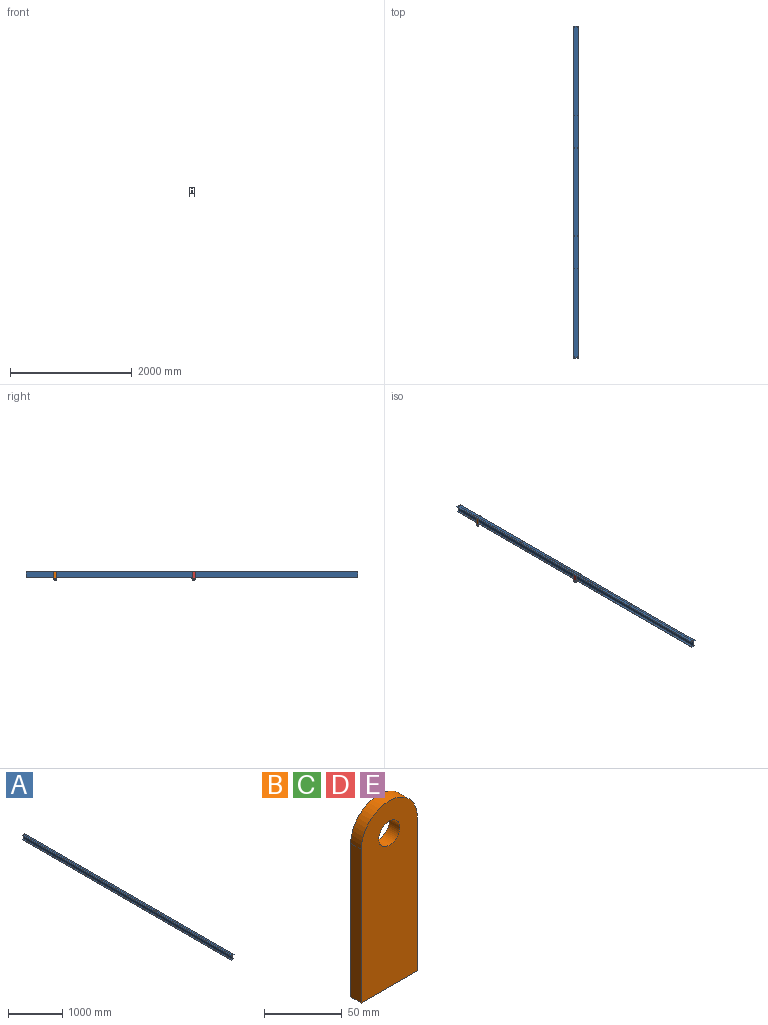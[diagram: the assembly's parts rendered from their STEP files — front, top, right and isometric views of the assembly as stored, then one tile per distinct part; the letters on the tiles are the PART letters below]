
ASSEMBLY  parts=5 mates=4
PART A: 26 faces, bbox 76.2x5448.3x101.6 mm
  f0: plane 5448.3x76.2mm, normal (0,0,1), area 414566.7mm2, adj f1,f11,f12,f13,f14,f15,f16,f17
  f1: plane 5448.3x4.32mm, normal (-1,0,0), area 23525.8mm2, adj f0,f2,f12,f13
  f2: plane 5448.3x35.94mm, normal (0,0,-1), area 195520.5mm2, adj f1,f3,f12,f13,f20,f21,f22,f23
  f3: plane 5448.3x92.96mm, normal (-1,0,0), area 506495.8mm2, adj f2,f4,f12,f13
  f4: plane 5448.3x32.23mm, normal (0,0,1), area 175618.2mm2, adj f3,f5,f12,f13
  f5: plane 5448.3x4.32mm, normal (-1,0,0), area 23525.8mm2, adj f4,f6,f12,f13
  f6: plane 5448.3x68.79mm, normal (0,0,-1), area 374762.1mm2, adj f5,f7,f12,f13
  f7: plane 5448.3x4.32mm, normal (1,0,0), area 23525.8mm2, adj f6,f8,f12,f13
  f8: plane 5448.3x32.23mm, normal (0,0,1), area 175618.2mm2, adj f7,f9,f12,f13
  f9: plane 5448.3x92.96mm, normal (1,0,0), area 506495.8mm2, adj f8,f10,f12,f13
  f10: plane 5448.3x35.94mm, normal (0,0,-1), area 195520.5mm2, adj f9,f11,f12,f13,f14,f15,f16,f17
  f11: plane 5448.3x4.32mm, normal (1,0,0), area 23525.8mm2, adj f0,f10,f12,f13
  f12: plane 101.6x76.2mm, normal (0,-1,0), area 1027.5mm2, adj f0,f1,f2,f3,f4,f5,f6,f7
  f13: plane 101.6x76.2mm, normal (0,1,0), area 1027.5mm2, adj f0,f1,f2,f3,f4,f5,f6,f7
  f14: cylinder r=3.97mm len=7.94mm, axis (0,0,1), area 107.7mm2, adj f0,f10
  f15: cylinder r=3.97mm len=7.94mm, axis (0,0,1), area 107.7mm2, adj f0,f10
  f16: cylinder r=3.97mm len=7.94mm, axis (0,0,1), area 107.7mm2, adj f0,f10
  f17: cylinder r=3.97mm len=7.94mm, axis (0,0,1), area 107.7mm2, adj f0,f10
  f18: cylinder r=3.97mm len=7.94mm, axis (0,0,1), area 107.7mm2, adj f0,f10
  f19: cylinder r=3.97mm len=7.94mm, axis (0,0,1), area 107.7mm2, adj f0,f10
  f20: cylinder r=3.97mm len=7.94mm, axis (0,0,1), area 107.7mm2, adj f0,f2
  f21: cylinder r=3.97mm len=7.94mm, axis (0,0,1), area 107.7mm2, adj f0,f2
  f22: cylinder r=3.97mm len=7.94mm, axis (0,0,1), area 107.7mm2, adj f0,f2
  f23: cylinder r=3.97mm len=7.94mm, axis (0,0,1), area 107.7mm2, adj f0,f2
  f24: cylinder r=3.97mm len=7.94mm, axis (0,0,1), area 107.7mm2, adj f0,f2
  f25: cylinder r=3.97mm len=7.94mm, axis (0,0,1), area 107.7mm2, adj f0,f2
PART B: 7 faces, bbox 50.8x9.5x146.1 mm
  f0: plane 120.65x9.53mm, normal (-1,0,0), area 1149.2mm2, adj f1,f4,f5,f6
  f1: plane 50.8x9.53mm, normal (0,0,-1), area 483.9mm2, adj f0,f2,f5,f6
  f2: plane 120.65x9.53mm, normal (1,0,0), area 1149.2mm2, adj f1,f4,f5,f6
  f3: cylinder r=9.53mm len=19.05mm, axis (0,1,0), area 570mm2, adj f5,f6
  f4: cylinder r=25.4mm len=50.8mm, axis (0,1,0), area 760.1mm2, adj f0,f2,f5,f6
  f5: plane 146.05x50.8mm, normal (0,-1,0), area 6857.4mm2, adj f0,f1,f2,f3,f4
  f6: plane 146.05x50.8mm, normal (0,1,0), area 6857.4mm2, adj f0,f1,f2,f3,f4
PART C: same geometry as B
PART D: same geometry as B
PART E: same geometry as B
PLACE A t=(-194.12,2841.14,122.51)mm
PLACE B rot(axis=(0.71,-0.71,0),180deg) t=(-255.18,2189.82,192.01)mm
PLACE C rot(axis=(0.71,0.71,0),180deg) t=(-159.93,2527.25,192.01)mm
PLACE D rot(axis=(0.71,-0.71,0),180deg) t=(-255.18,-77.13,192.01)mm
PLACE E rot(axis=(0.71,0.71,0),180deg) t=(-159.93,260.3,189.85)mm
MATE fastened E.f5 <-> A.f11  axis (-1,0,0) through (-169.45,116.99,146.69)mm
MATE fastened B.f5 <-> A.f1  axis (1,0,0) through (-245.65,2383.94,148.85)mm
MATE fastened C.f5 <-> A.f11  axis (-1,0,0) through (-169.45,2383.94,148.85)mm
MATE fastened D.f5 <-> A.f1  axis (1,0,0) through (-245.65,116.99,148.85)mm
